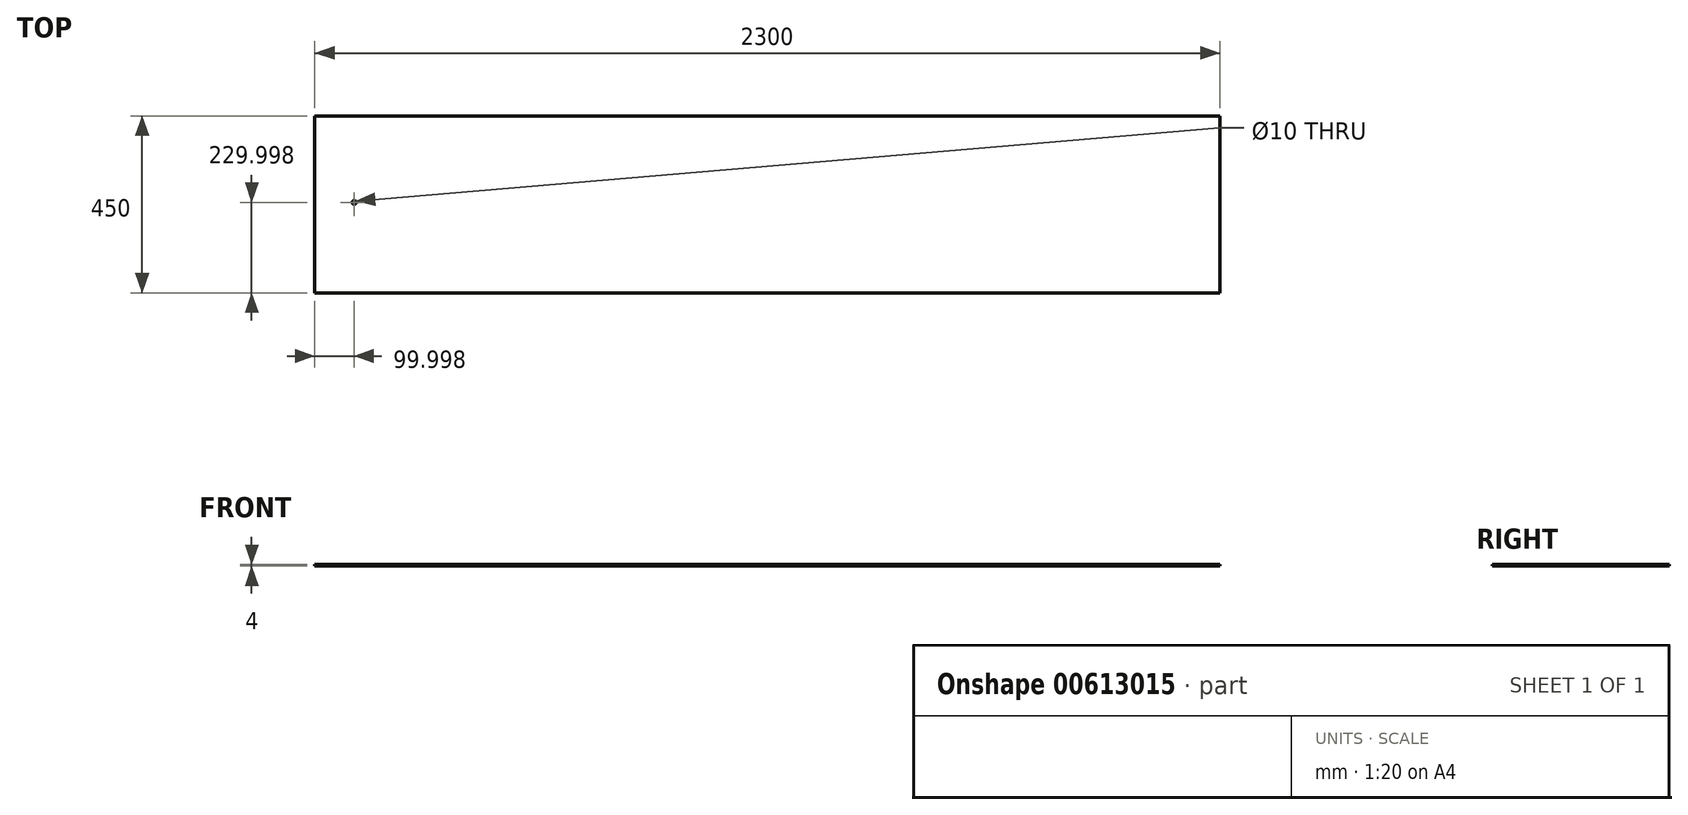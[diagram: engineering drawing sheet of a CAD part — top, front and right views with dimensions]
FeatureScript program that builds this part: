
annotation { "Feature Type Name" : "Feature", "Feature Type Description" : "" }
export const myFeature = defineFeature(function(context is Context, id is Id, definition is map)
    precondition{}
    {
        {
            var Q0;
            Q0=qCreatedBy(makeId("Top.planeOp"),FACE);
            var sketch = newSketch(context, id + "F0", { "sketchPlane" : qUnion([Q0])});
            skLineSegment(sketch, "E0.bottom", {"start": v(1940, -192.73) * mm, "end": v(-360, -192.73) * mm});
            skLineSegment(sketch, "E0.top", {"start": v(1940, 257.27) * mm, "end": v(-360, 257.27) * mm});
            skLineSegment(sketch, "E0.left", {"start": v(1940, -192.73) * mm, "end": v(1940, 257.27) * mm});
            skLineSegment(sketch, "E0.right", {"start": v(-360, -192.73) * mm, "end": v(-360, 257.27) * mm});
            skPoint(sketch, "E0.middle", {"position": v(790, 32.27) * mm});
            skCircle(sketch, "E1", {"center": v(-260, 37.27) * mm, "radius": 5 * mm});
            skSolve(sketch);
        }
        {
            var Q0;
            Q0 = qSketchRegion(id + "F0", true);
            extrude(context, id + "F1", {"entities" : qUnion([Q0]), "depth" : 4 * mm, "offsetDistance" : 25 * mm});
        }
    });
